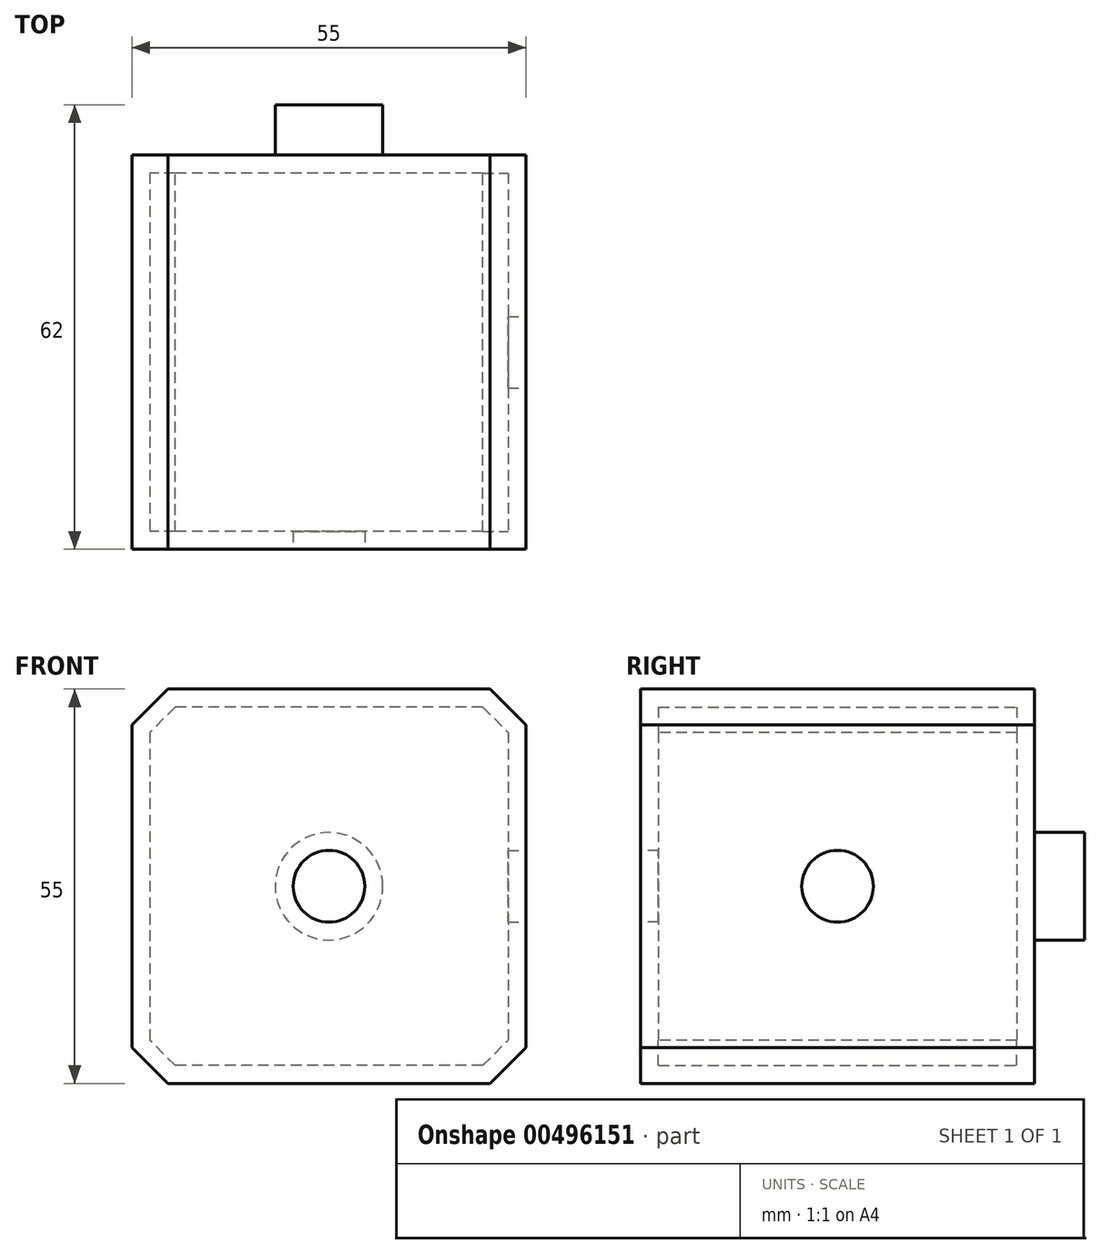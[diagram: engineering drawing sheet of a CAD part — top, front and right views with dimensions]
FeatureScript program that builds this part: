
annotation { "Feature Type Name" : "Feature", "Feature Type Description" : "" }
export const myFeature = defineFeature(function(context is Context, id is Id, definition is map)
    precondition{}
    {
        {
            var Q0;
            Q0=qCreatedBy(makeId("Front.planeOp"),FACE);
            var sketch = newSketch(context, id + "F0", { "sketchPlane" : qUnion([Q0])});
            skLineSegment(sketch, "E0.bottom", {"start": v(27.5, 27.5) * mm, "end": v(-27.5, 27.5) * mm});
            skLineSegment(sketch, "E0.top", {"start": v(27.5, -27.5) * mm, "end": v(-27.5, -27.5) * mm});
            skLineSegment(sketch, "E0.left", {"start": v(27.5, 27.5) * mm, "end": v(27.5, -27.5) * mm});
            skLineSegment(sketch, "E0.right", {"start": v(-27.5, 27.5) * mm, "end": v(-27.5, -27.5) * mm});
            skPoint(sketch, "E0.middle", {"position": v(0, 0) * mm});
            skSolve(sketch);
        }
        {
            var Q0;
            Q0 = qSketchRegion(id + "F0", true);
            extrude(context, id + "F1", {"entities" : qUnion([Q0]), "depth" : 55 * mm});
        }
        {
            var Q0;
            Q0=makeQuery(id+"F1.opExtrude","SWEPT_EDGE",EDGE,{"disambiguationData":[OSD([sQuery(id+"F0.wireOp",EDGE,"E0.bottom"),sQuery(id+"F0.wireOp",EDGE,"E0.left")])]});
            var Q1;
            Q1=makeQuery(id+"F1.opExtrude","SWEPT_EDGE",EDGE,{"disambiguationData":[OSD([sQuery(id+"F0.wireOp",EDGE,"E0.bottom"),sQuery(id+"F0.wireOp",EDGE,"E0.right")])]});
            var Q2;
            Q2=makeQuery(id+"F1.opExtrude","SWEPT_EDGE",EDGE,{"disambiguationData":[OSD([sQuery(id+"F0.wireOp",EDGE,"E0.top"),sQuery(id+"F0.wireOp",EDGE,"E0.left")])]});
            var Q3;
            Q3=makeQuery(id+"F1.opExtrude","SWEPT_EDGE",EDGE,{"disambiguationData":[OSD([sQuery(id+"F0.wireOp",EDGE,"E0.top"),sQuery(id+"F0.wireOp",EDGE,"E0.right")])]});
            chamfer(context, id + "F2", {"entities" : qUnion([Q0, Q1, Q2, Q3]), "width" : 5 * mm, "tangentPropagation" : true});
        }
        {
            var Q0;
            Q0=makeQuery(id+"F1.opExtrude","CAP_FACE",FACE,{"disambiguationData":[OSD([sQuery(id+"F0.wireOp",EDGE,"E0.bottom"),sQuery(id+"F0.wireOp",EDGE,"E0.top"),sQuery(id+"F0.wireOp",EDGE,"E0.left"),sQuery(id+"F0.wireOp",EDGE,"E0.right")])],"isStart":false});
            var sketch = newSketch(context, id + "F3", { "sketchPlane" : qUnion([Q0])});
            skCircle(sketch, "E1", {"center": v(0, 0) * mm, "radius": 5 * mm});
            skSolve(sketch);
        }
        {
            var Q0;
            Q0=makeQuery(id+"F1.opExtrude","SWEPT_FACE",FACE,{"disambiguationData":[OSD([sQuery(id+"F0.wireOp",EDGE,"E0.left")])]});
            var sketch = newSketch(context, id + "F4", { "sketchPlane" : qUnion([Q0])});
            skCircle(sketch, "E2", {"center": v(-27.5, 0) * mm, "radius": 5 * mm});
            skPoint(sketch, "E2.centerSnap0", {"position": v(-27.5, 22.5) * mm});
            skSolve(sketch);
        }
        {
            var Q0;
            Q0=makeQuery(id+"F1.opExtrude","CAP_FACE",FACE,{"disambiguationData":[OSD([sQuery(id+"F0.wireOp",EDGE,"E0.bottom"),sQuery(id+"F0.wireOp",EDGE,"E0.top"),sQuery(id+"F0.wireOp",EDGE,"E0.left"),sQuery(id+"F0.wireOp",EDGE,"E0.right")])],"isStart":false});
            shell(context, id + "F5", {"entities" : qUnion([Q0]), "thickness" : 2.5 * mm});
        }
        {
            var Q0;
            Q0=makeQuery(id+"F3.imprint","IMPRINT",FACE,{"disambiguationData":[TD([[makeQuery(id+"F3.imprint","IMPRINT",EDGE,{"derivedFrom":sQuery(id+"F3.wireOp",EDGE,"E1")}),-1.0]])]});
            var sketch = newSketch(context, id + "F6", { "sketchPlane" : qUnion([Q0])});
            skLineSegment(sketch, "E3.bottom", {"start": v(22.5, 27.5) * mm, "end": v(-22.5, 27.5) * mm});
            skLineSegment(sketch, "E3.top", {"start": v(22.5, -27.5) * mm, "end": v(-22.5, -27.5) * mm});
            skLineSegment(sketch, "E3.left", {"start": v(27.5, 22.5) * mm, "end": v(27.5, -22.5) * mm});
            skLineSegment(sketch, "E3.right", {"start": v(-27.5, 22.5) * mm, "end": v(-27.5, -22.5) * mm});
            skPoint(sketch, "E3.middle", {"position": v(0, 0) * mm});
            skLineSegment(sketch, "E4", {"start": v(-22.5, 27.5) * mm, "end": v(-27.5, 22.5) * mm});
            skLineSegment(sketch, "E5", {"start": v(-22.5, -27.5) * mm, "end": v(-27.5, -22.5) * mm});
            skLineSegment(sketch, "E6", {"start": v(22.5, -27.5) * mm, "end": v(27.5, -22.5) * mm});
            skLineSegment(sketch, "E7", {"start": v(27.5, 22.5) * mm, "end": v(22.5, 27.5) * mm});
            skSolve(sketch);
        }
        {
            var Q0;
            Q0 = qSketchRegion(id + "F6", true);
            extrude(context, id + "F7", {"entities" : qUnion([Q0]), "operationType" : NewBodyOperationType.ADD, "oppositeDirection" : true, "depth" : 2.5 * mm});
        }
        {
            var Q0;
            Q0 = qSketchRegion(id + "F4", true);
            extrude(context, id + "F8", {"entities" : qUnion([Q0]), "operationType" : NewBodyOperationType.REMOVE, "oppositeDirection" : true, "depth" : 2.5 * mm});
        }
        {
            var Q0;
            Q0 = qSketchRegion(id + "F3", true);
            extrude(context, id + "F9", {"entities" : qUnion([Q0]), "operationType" : NewBodyOperationType.REMOVE, "oppositeDirection" : true, "depth" : 2.5 * mm});
        }
        {
            var Q0;
            Q0=makeQuery(id+"F1.opExtrude","CAP_FACE",FACE,{"disambiguationData":[OSD([sQuery(id+"F0.wireOp",EDGE,"E0.bottom"),sQuery(id+"F0.wireOp",EDGE,"E0.top"),sQuery(id+"F0.wireOp",EDGE,"E0.left"),sQuery(id+"F0.wireOp",EDGE,"E0.right")])],"isStart":true});
            var sketch = newSketch(context, id + "F10", { "sketchPlane" : qUnion([Q0])});
            skCircle(sketch, "E8", {"center": v(0, 0) * mm, "radius": 7.5 * mm});
            skSolve(sketch);
        }
        {
            var Q0;
            Q0 = qSketchRegion(id + "F10", true);
            extrude(context, id + "F11", {"entities" : qUnion([Q0]), "operationType" : NewBodyOperationType.ADD, "depth" : 7 * mm});
        }
    });
